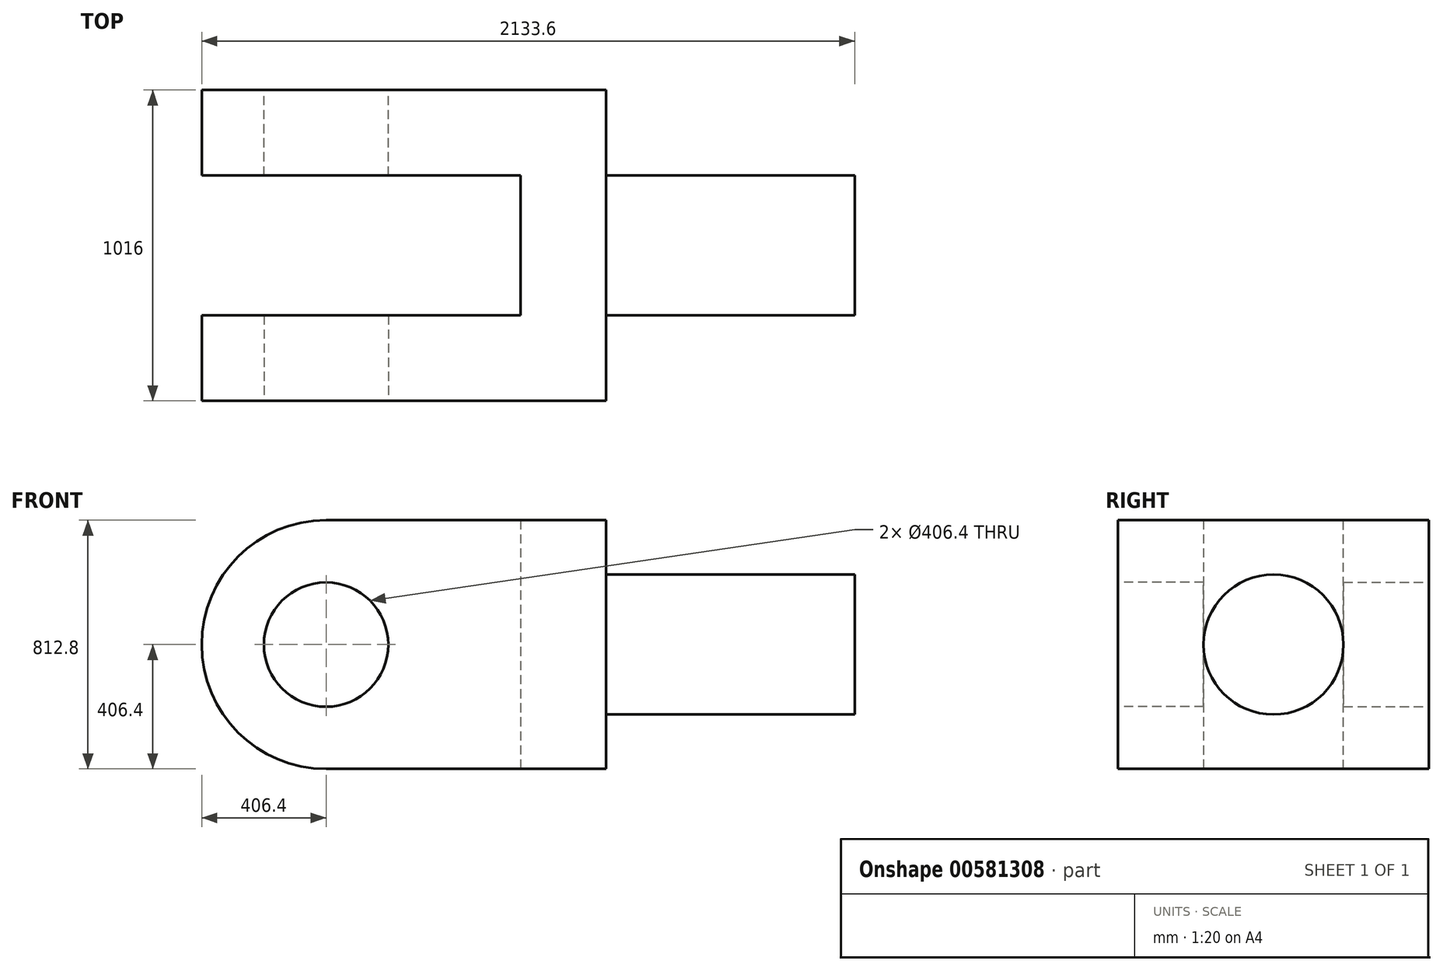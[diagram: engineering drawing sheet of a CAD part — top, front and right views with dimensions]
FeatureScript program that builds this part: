
annotation { "Feature Type Name" : "Feature", "Feature Type Description" : "" }
export const myFeature = defineFeature(function(context is Context, id is Id, definition is map)
    precondition{}
    {
        {
            var Q0;
            Q0=qCreatedBy(makeId("Right.planeOp"),FACE);
            var sketch = newSketch(context, id + "F0", { "sketchPlane" : qUnion([Q0])});
            skCircle(sketch, "E0", {"center": v(0, 0) * mm, "radius": 228.6 * mm});
            skSolve(sketch);
        }
        {
            var Q0;
            Q0 = qSketchRegion(id + "F0", true);
            extrude(context, id + "F1", {"entities" : qUnion([Q0]), "depth" : 812.8 * mm, "offsetDistance" : 25.4 * mm});
        }
        {
            var Q0;
            Q0=qCreatedBy(makeId("Top.planeOp"),FACE);
            var sketch = newSketch(context, id + "F2", { "sketchPlane" : qUnion([Q0])});
            skLineSegment(sketch, "E1", {"start": v(0, 0) * mm, "end": v(0, -508) * mm});
            skLineSegment(sketch, "E2", {"start": v(0, 0) * mm, "end": v(0, 508) * mm});
            skLineSegment(sketch, "E3", {"start": v(0, 508) * mm, "end": v(-914.4, 508) * mm});
            skLineSegment(sketch, "E4", {"start": v(-914.4, 508) * mm, "end": v(-914.4, 228.6) * mm});
            skLineSegment(sketch, "E5", {"start": v(-914.4, 228.6) * mm, "end": v(-279.4, 228.6) * mm});
            skLineSegment(sketch, "E6", {"start": v(-279.4, 228.6) * mm, "end": v(-279.4, -228.6) * mm});
            skLineSegment(sketch, "E7", {"start": v(-279.4, -228.6) * mm, "end": v(-914.4, -228.6) * mm});
            skLineSegment(sketch, "E8", {"start": v(-914.4, -228.6) * mm, "end": v(-914.4, -508) * mm});
            skLineSegment(sketch, "E9", {"start": v(-914.4, -508) * mm, "end": v(0, -508) * mm});
            skSolve(sketch);
        }
        {
            var Q0;
            Q0=makeQuery(id+"F2.imprint","IMPRINT",FACE,{"disambiguationData":[TD([[makeQuery(id+"F2.imprint","IMPRINT",EDGE,{"derivedFrom":sQuery(id+"F2.wireOp",EDGE,"E1")}),-1.0]])]});
            extrude(context, id + "F3", {"entities" : qUnion([Q0]), "operationType" : NewBodyOperationType.ADD, "depth" : 406.4 * mm, "offsetDistance" : 25.4 * mm});
        }
        {
            var Q0;
            Q0=makeQuery(id+"F3.opExtrude","CAP_FACE",FACE,{"disambiguationData":[OSD([sQuery(id+"F2.wireOp",EDGE,"E1"),sQuery(id+"F2.wireOp",EDGE,"E2"),sQuery(id+"F2.wireOp",EDGE,"E3"),sQuery(id+"F2.wireOp",EDGE,"E4"),sQuery(id+"F2.wireOp",EDGE,"E5"),sQuery(id+"F2.wireOp",EDGE,"E6"),sQuery(id+"F2.wireOp",EDGE,"E7"),sQuery(id+"F2.wireOp",EDGE,"E8"),sQuery(id+"F2.wireOp",EDGE,"E9")])],"isStart":true});
            extrude(context, id + "F4", {"entities" : qUnion([Q0]), "operationType" : NewBodyOperationType.ADD, "depth" : 406.4 * mm, "offsetDistance" : 25.4 * mm});
        }
        {
            var Q0;
            {var subQ0=sQuery(id+"F2.wireOp",EDGE,"E9");Q0=makeQuery(id+"F4.boolean.opBoolean","MERGE",FACE,{"derivedFrom":[makeQuery(id+"F3.opExtrude","SWEPT_FACE",FACE,{"disambiguationData":[OSD([subQ0])]}),makeQuery(id+"F4.opExtrude","SWEPT_FACE",FACE,{"disambiguationData":[OSD([subQ0])]})]});}
            var sketch = newSketch(context, id + "F5", { "sketchPlane" : qUnion([Q0])});
            skCircle(sketch, "E10", {"center": v(-914.4, 0) * mm, "radius": 406.4 * mm});
            skSolve(sketch);
        }
        {
            var Q0;
            {var subQ1=sQuery(id+"F2.wireOp",EDGE,"E9");var subQ2=sQuery(id+"F2.wireOp",EDGE,"E8");var subQ3=makeQuery(id+"F4.boolean.opBoolean","MERGE",EDGE,{"derivedFrom":[makeQuery(id+"F3.opExtrude","SWEPT_EDGE",EDGE,{"disambiguationData":[OSD([subQ2,subQ1])]}),makeQuery(id+"F4.opExtrude","SWEPT_EDGE",EDGE,{"disambiguationData":[OSD([subQ2,subQ1])]})]});Q0=makeQuery(id+"F5.imprint","IMPRINT",FACE,{"disambiguationData":[TD([[makeQuery(id+"F5.imprint","IMPRINT",EDGE,{"derivedFrom":subQ3}),-1.0]])]});}
            extrude(context, id + "F6", {"entities" : qUnion([Q0]), "operationType" : NewBodyOperationType.ADD, "oppositeDirection" : true, "depth" : 279.4 * mm, "offsetDistance" : 25.4 * mm});
        }
        {
            var Q0;
            {var subQ0=sQuery(id+"F2.wireOp",EDGE,"E3");Q0=makeQuery(id+"F4.boolean.opBoolean","MERGE",FACE,{"derivedFrom":[makeQuery(id+"F3.opExtrude","SWEPT_FACE",FACE,{"disambiguationData":[OSD([subQ0])]}),makeQuery(id+"F4.opExtrude","SWEPT_FACE",FACE,{"disambiguationData":[OSD([subQ0])]})]});}
            var sketch = newSketch(context, id + "F7", { "sketchPlane" : qUnion([Q0])});
            skCircle(sketch, "E11", {"center": v(914.4, 0) * mm, "radius": 406.4 * mm});
            skSolve(sketch);
        }
        {
            var Q0;
            {var subQ1=sQuery(id+"F2.wireOp",EDGE,"E4");var subQ2=sQuery(id+"F2.wireOp",EDGE,"E3");var subQ3=makeQuery(id+"F4.boolean.opBoolean","MERGE",EDGE,{"derivedFrom":[makeQuery(id+"F3.opExtrude","SWEPT_EDGE",EDGE,{"disambiguationData":[OSD([subQ2,subQ1])]}),makeQuery(id+"F4.opExtrude","SWEPT_EDGE",EDGE,{"disambiguationData":[OSD([subQ2,subQ1])]})]});Q0=makeQuery(id+"F7.imprint","IMPRINT",FACE,{"disambiguationData":[TD([[makeQuery(id+"F7.imprint","IMPRINT",EDGE,{"derivedFrom":subQ3}),1.0]])]});}
            extrude(context, id + "F8", {"entities" : qUnion([Q0]), "operationType" : NewBodyOperationType.ADD, "oppositeDirection" : true, "depth" : 279.4 * mm, "offsetDistance" : 25.4 * mm});
        }
        {
            var Q0;
            {var subQ0=sQuery(id+"F2.wireOp",EDGE,"E9");Q0=makeQuery(id+"F6.boolean.opBoolean","MERGE",FACE,{"derivedFrom":[makeQuery(id+"F4.boolean.opBoolean","MERGE",FACE,{"derivedFrom":[makeQuery(id+"F3.opExtrude","SWEPT_FACE",FACE,{"disambiguationData":[OSD([subQ0])]}),makeQuery(id+"F4.opExtrude","SWEPT_FACE",FACE,{"disambiguationData":[OSD([subQ0])]})]}),makeQuery(id+"F6.opExtrude","CAP_FACE",FACE,{"disambiguationData":[OSD([sQuery(id+"F2.wireOp",EDGE,"E8"),subQ0,sQuery(id+"F5.wireOp",EDGE,"E10")])],"isStart":true})]});}
            var sketch = newSketch(context, id + "F9", { "sketchPlane" : qUnion([Q0])});
            skCircle(sketch, "E12", {"center": v(-914.4, 0) * mm, "radius": 203.2 * mm});
            skSolve(sketch);
        }
        {
            var Q0;
            Q0=makeQuery(id+"F9.imprint","IMPRINT",FACE,{"disambiguationData":[TD([[makeQuery(id+"F9.imprint","IMPRINT",EDGE,{"derivedFrom":sQuery(id+"F9.wireOp",EDGE,"E12")}),1.0]])]});
            extrude(context, id + "F10", {"entities" : qUnion([Q0]), "operationType" : NewBodyOperationType.REMOVE, "oppositeDirection" : true, "depth" : 279.4 * mm, "offsetDistance" : 25.4 * mm});
        }
        {
            var Q0;
            {var subQ0=sQuery(id+"F2.wireOp",EDGE,"E3");Q0=makeQuery(id+"F8.boolean.opBoolean","MERGE",FACE,{"derivedFrom":[makeQuery(id+"F4.boolean.opBoolean","MERGE",FACE,{"derivedFrom":[makeQuery(id+"F3.opExtrude","SWEPT_FACE",FACE,{"disambiguationData":[OSD([subQ0])]}),makeQuery(id+"F4.opExtrude","SWEPT_FACE",FACE,{"disambiguationData":[OSD([subQ0])]})]}),makeQuery(id+"F8.opExtrude","CAP_FACE",FACE,{"disambiguationData":[OSD([subQ0,sQuery(id+"F2.wireOp",EDGE,"E4"),sQuery(id+"F7.wireOp",EDGE,"E11")])],"isStart":true})]});}
            var sketch = newSketch(context, id + "F11", { "sketchPlane" : qUnion([Q0])});
            skCircle(sketch, "E13", {"center": v(914.4, 0) * mm, "radius": 203.2 * mm});
            skSolve(sketch);
        }
        {
            var Q0;
            Q0=makeQuery(id+"F11.imprint","IMPRINT",FACE,{"disambiguationData":[TD([[makeQuery(id+"F11.imprint","IMPRINT",EDGE,{"derivedFrom":sQuery(id+"F11.wireOp",EDGE,"E13")}),1.0]])]});
            extrude(context, id + "F12", {"entities" : qUnion([Q0]), "operationType" : NewBodyOperationType.REMOVE, "oppositeDirection" : true, "depth" : 279.4 * mm, "offsetDistance" : 25.4 * mm});
        }
    });
